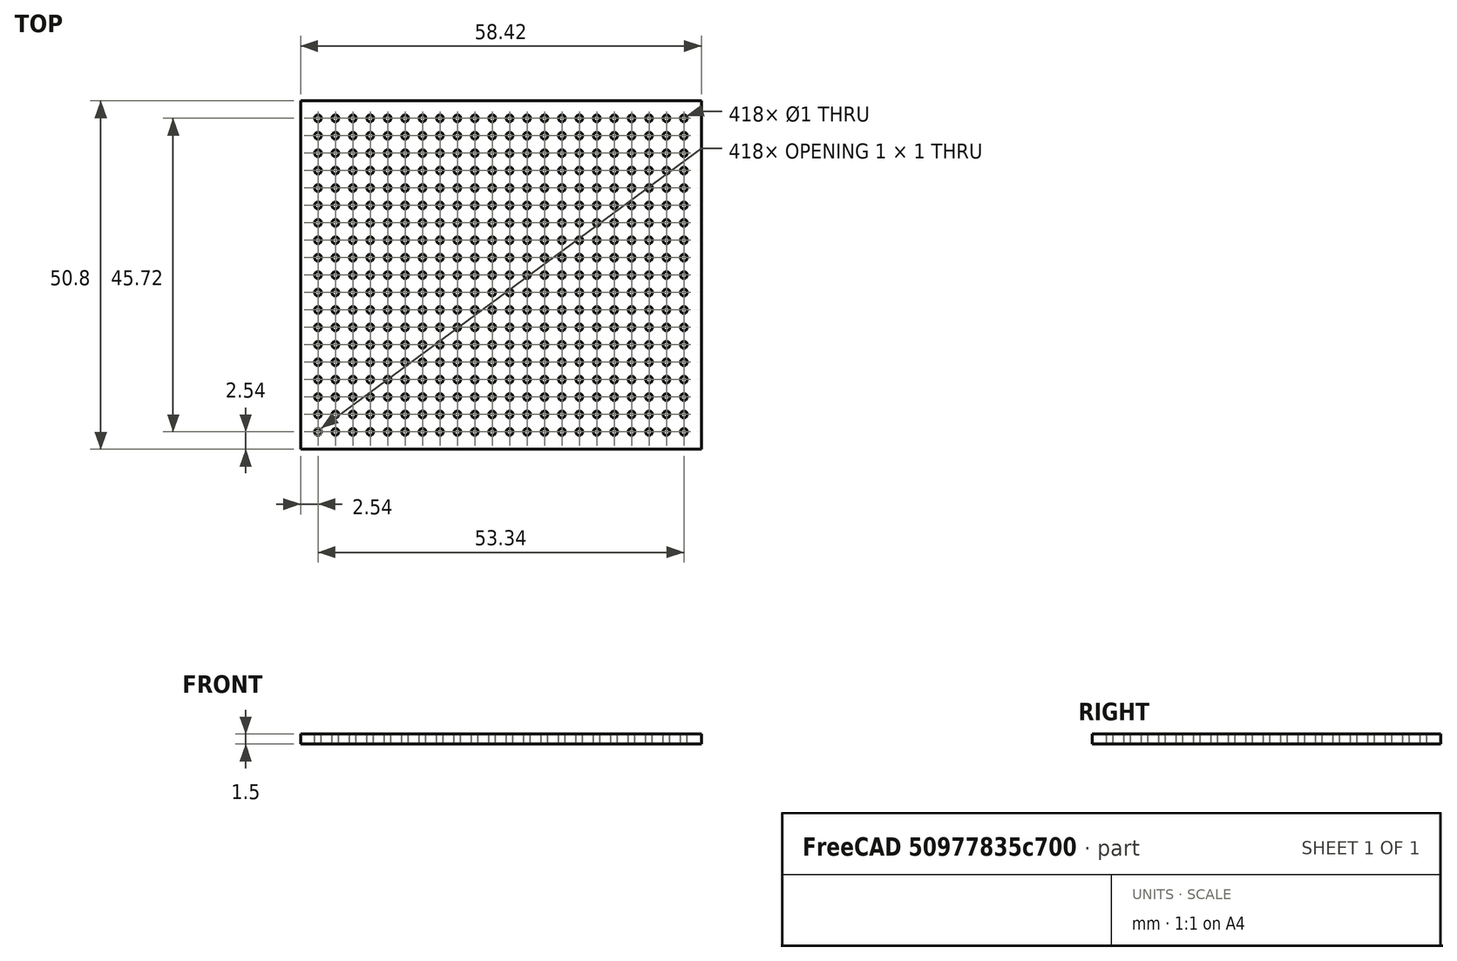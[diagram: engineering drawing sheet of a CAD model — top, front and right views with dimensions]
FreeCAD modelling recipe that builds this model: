
FCSTD DOCUMENT  (FreeCAD 0.14R3692 (Git))
Label: PrefBoard
License: CC-BY 3.0
LicenseURL: http://creativecommons.org/licenses/by/3.0/
objects: Part::Box×1, Part::Cylinder×1, Part::FeaturePython×1, Part::Cut×1
note: 4 computed .brp shape members not serialized (recipe doc carries the construction recipe); baked Part::Feature solids carry a one-line shape summary decoded from their .brp

FEATURE [Part::Box] Box  label="BoardCube"
  Height = 1.5
  Length = 58.42
  Width = 50.8
FEATURE [Part::Cylinder] Cylinder  label="HoleCylinder"
  Angle = 360
  Height = 2.5
  Placement = pos=(2.54,2.54,-0.5) rot=(0,0,1;0rad)
  Radius = 0.5
FEATURE [Part::FeaturePython] Array  label="HoleArray"  # Draft array (typed FeaturePython)
  Angle = 360
  ArrayType = 0
  Axis = (0,0,1)
  Base = -> Cylinder
  Center = (0,0,0)
  IntervalX = (2.54,0,0)
  IntervalY = (0,2.54,0)
  IntervalZ = (0,0,1)
  NumberPolar = 1
  NumberX = 22
  NumberY = 19
  NumberZ = 1
FEATURE [Part::Cut] Cut  label="BoardCut"
  Base = -> Box
  Tool = -> Array
